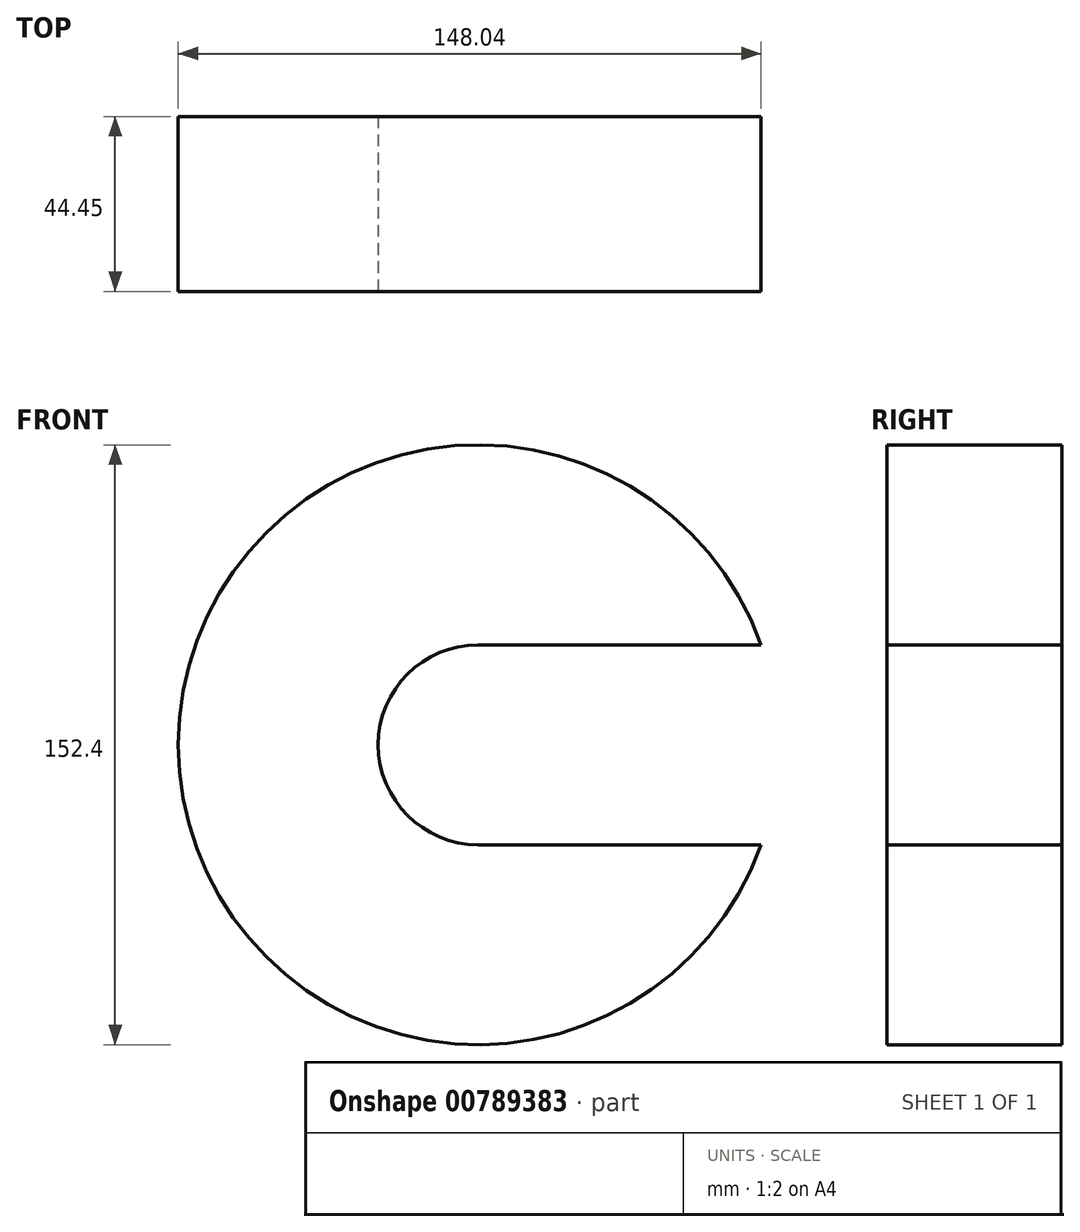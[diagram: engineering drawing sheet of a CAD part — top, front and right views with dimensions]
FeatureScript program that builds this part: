
annotation { "Feature Type Name" : "Feature", "Feature Type Description" : "" }
export const myFeature = defineFeature(function(context is Context, id is Id, definition is map)
    precondition{}
    {
        {
            var Q0;
            Q0=qCreatedBy(makeId("Front.planeOp"),FACE);
            var sketch = newSketch(context, id + "F0", { "sketchPlane" : qUnion([Q0])});
            skCircle(sketch, "E0", {"center": v(0, 0) * mm, "radius": 76.2 * mm});
            skSolve(sketch);
        }
        {
            var Q0;
            Q0=makeQuery(id+"F0.imprint","IMPRINT",FACE,{"disambiguationData":[TD([[makeQuery(id+"F0.imprint","IMPRINT",EDGE,{"derivedFrom":sQuery(id+"F0.wireOp",EDGE,"E0")}),1.0]])]});
            extrude(context, id + "F1", {"entities" : qUnion([Q0]), "depth" : 44.45 * mm, "offsetDistance" : 25.4 * mm});
        }
        {
            var Q0;
            Q0=makeQuery(id+"F1.opExtrude","CAP_FACE",FACE,{"disambiguationData":[OSD([sQuery(id+"F0.wireOp",EDGE,"E0")])],"isStart":false});
            var sketch = newSketch(context, id + "F2", { "sketchPlane" : qUnion([Q0])});
            skArc(sketch, "E1", {"start": v(0, 25.4) * mm, "mid": v(-25.4, 0) * mm, "end": v(0, -25.4) * mm});
            skArc(sketch, "E2", {"start": v(71.84, -25.4) * mm, "mid": v(76.2, 0) * mm, "end": v(71.84, 25.4) * mm});
            skLineSegment(sketch, "E3", {"start": v(0, 25.4) * mm, "end": v(71.84, 25.4) * mm});
            skLineSegment(sketch, "E4", {"start": v(71.84, 25.4) * mm, "end": v(71.84, 25.4) * mm});
            skLineSegment(sketch, "E5", {"start": v(0, -25.4) * mm, "end": v(71.84, -25.4) * mm});
            skSolve(sketch);
        }
        {
            var Q0;
            Q0=makeQuery(id+"F2.imprint","IMPRINT",FACE,{"disambiguationData":[TD([[makeQuery(id+"F2.imprint","IMPRINT",EDGE,{"derivedFrom":sQuery(id+"F2.wireOp",EDGE,"E1")}),1.0]])]});
            var Q1;
            Q1=sQuery(id+"F2.wireOp",EDGE,"E3");
            var Q2;
            Q2=sQuery(id+"F2.wireOp",EDGE,"E2");
            var Q3;
            Q3=sQuery(id+"F2.wireOp",EDGE,"E5");
            var Q4;
            Q4=sQuery(id+"F2.wireOp",EDGE,"E1");
            extrude(context, id + "F3", {"entities" : qUnion([Q0]), "operationType" : NewBodyOperationType.REMOVE, "surfaceEntities" : qUnion([Q1, Q2, Q3, Q4]), "endBound" : BoundingType.UP_TO_NEXT, "oppositeDirection" : true, "depth" : 25.4 * mm, "offsetDistance" : 25.4 * mm});
        }
    });
